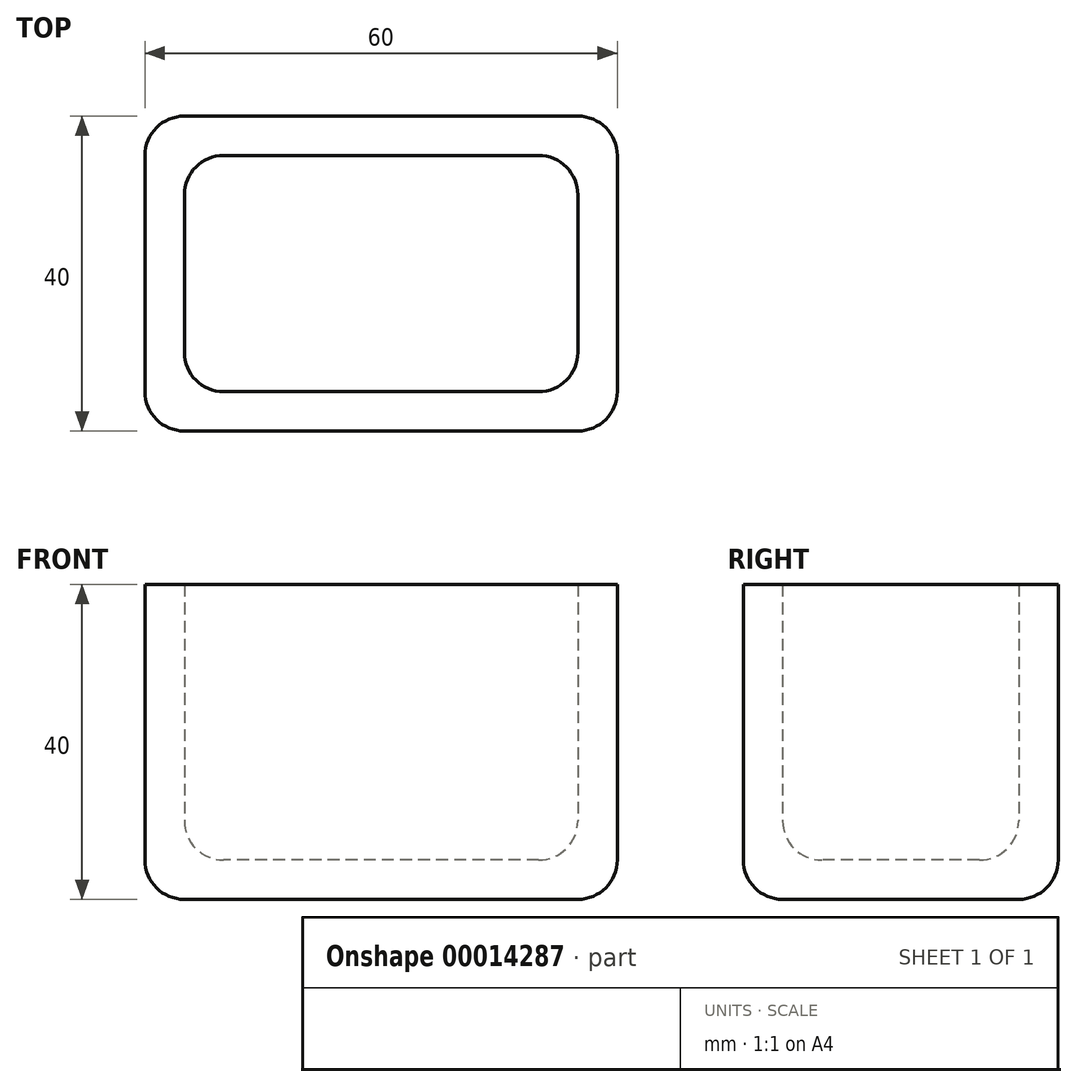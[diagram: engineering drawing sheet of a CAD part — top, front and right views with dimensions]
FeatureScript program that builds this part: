
annotation { "Feature Type Name" : "Feature", "Feature Type Description" : "" }
export const myFeature = defineFeature(function(context is Context, id is Id, definition is map)
    precondition{}
    {
        {
            var Q0;
            Q0=qCreatedBy(makeId("Top.planeOp"),FACE);
            var sketch = newSketch(context, id + "F0", { "sketchPlane" : qUnion([Q0])});
            skLineSegment(sketch, "E0.rect.bottom", {"start": v(30, 20) * mm, "end": v(-30, 20) * mm});
            skLineSegment(sketch, "E0.rect.top", {"start": v(30, -20) * mm, "end": v(-30, -20) * mm});
            skLineSegment(sketch, "E0.rect.left", {"start": v(30, 20) * mm, "end": v(30, -20) * mm});
            skLineSegment(sketch, "E0.rect.right", {"start": v(-30, 20) * mm, "end": v(-30, -20) * mm});
            skPoint(sketch, "E0.rect.middle", {"position": v(0, 0) * mm});
            skSolve(sketch);
        }
        {
            var Q0;
            Q0=makeQuery(id+"F0.imprint","IMPRINT",FACE,{"disambiguationData":[TD([[makeQuery(id+"F0.imprint","IMPRINT",EDGE,{"derivedFrom":sQuery(id+"F0.wireOp",EDGE,"E0.rect.bottom")}),1.0]])]});
            extrude(context, id + "F1", {"entities" : qUnion([Q0]), "depth" : 40 * mm});
        }
        {
            var Q0;
            Q0=makeQuery(id+"F1.opExtrude","CAP_FACE",FACE,{"disambiguationData":[OSD([sQuery(id+"F0.wireOp",EDGE,"E0.rect.bottom"),sQuery(id+"F0.wireOp",EDGE,"E0.rect.top"),sQuery(id+"F0.wireOp",EDGE,"E0.rect.left"),sQuery(id+"F0.wireOp",EDGE,"E0.rect.right")])],"isStart":false});
            shell(context, id + "F2", {"entities" : qUnion([Q0]), "thickness" : 5 * mm});
        }
        {
            var Q0;
            Q0=makeQuery(id+"F2.opShell","OFFSET_EDGE",EDGE,{"disambiguationData":[OSD([sQuery(id+"F0.wireOp",EDGE,"E0.rect.bottom"),sQuery(id+"F0.wireOp",EDGE,"E0.rect.left")])]});
            var Q1;
            Q1=makeQuery(id+"F2.opShell","OFFSET_EDGE",EDGE,{"disambiguationData":[OSD([sQuery(id+"F0.wireOp",EDGE,"E0.rect.bottom"),sQuery(id+"F0.wireOp",EDGE,"E0.rect.right")])]});
            var Q2;
            Q2=makeQuery(id+"F2.opShell","OFFSET_EDGE",EDGE,{"disambiguationData":[OSD([sQuery(id+"F0.wireOp",EDGE,"E0.rect.top"),sQuery(id+"F0.wireOp",EDGE,"E0.rect.right")])]});
            var Q3;
            Q3=makeQuery(id+"F2.opShell","OFFSET_EDGE",EDGE,{"disambiguationData":[OSD([sQuery(id+"F0.wireOp",EDGE,"E0.rect.top"),sQuery(id+"F0.wireOp",EDGE,"E0.rect.left")])]});
            var Q4;
            Q4=makeQuery(id+"F2.opShell","OFFSET_FACE",FACE,{"disambiguationData":[OSD([sQuery(id+"F0.wireOp",EDGE,"E0.rect.bottom"),sQuery(id+"F0.wireOp",EDGE,"E0.rect.top"),sQuery(id+"F0.wireOp",EDGE,"E0.rect.left"),sQuery(id+"F0.wireOp",EDGE,"E0.rect.right")])]});
            var Q5;
            Q5=makeQuery(id+"F1.opExtrude","SWEPT_EDGE",EDGE,{"disambiguationData":[OSD([sQuery(id+"F0.wireOp",EDGE,"E0.rect.top"),sQuery(id+"F0.wireOp",EDGE,"E0.rect.left")])]});
            var Q6;
            Q6=makeQuery(id+"F1.opExtrude","SWEPT_EDGE",EDGE,{"disambiguationData":[OSD([sQuery(id+"F0.wireOp",EDGE,"E0.rect.top"),sQuery(id+"F0.wireOp",EDGE,"E0.rect.right")])]});
            var Q7;
            Q7=makeQuery(id+"F1.opExtrude","SWEPT_EDGE",EDGE,{"disambiguationData":[OSD([sQuery(id+"F0.wireOp",EDGE,"E0.rect.bottom"),sQuery(id+"F0.wireOp",EDGE,"E0.rect.right")])]});
            var Q8;
            Q8=makeQuery(id+"F1.opExtrude","SWEPT_EDGE",EDGE,{"disambiguationData":[OSD([sQuery(id+"F0.wireOp",EDGE,"E0.rect.bottom"),sQuery(id+"F0.wireOp",EDGE,"E0.rect.left")])]});
            var Q9;
            Q9=makeQuery(id+"F1.opExtrude","CAP_FACE",FACE,{"disambiguationData":[OSD([sQuery(id+"F0.wireOp",EDGE,"E0.rect.bottom"),sQuery(id+"F0.wireOp",EDGE,"E0.rect.top"),sQuery(id+"F0.wireOp",EDGE,"E0.rect.left"),sQuery(id+"F0.wireOp",EDGE,"E0.rect.right")])],"isStart":true});
            fillet(context, id + "F3", {"entities" : qUnion([Q0, Q1, Q2, Q3, Q4, Q5, Q6, Q7, Q8, Q9]), "radius" : 5 * mm, "tangentPropagation" : true, "allowEdgeOverflow" : false});
        }
    });
